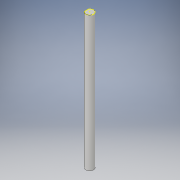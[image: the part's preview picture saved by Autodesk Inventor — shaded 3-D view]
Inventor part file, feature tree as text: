
AUTODESK INVENTOR PART (.ipt)
format: ipt  version: 2017 (Build 210142000, 142)  size: 114,688 bytes
history: native  units: in
note: dims shown in document units (in); Inventor stores cm internally (conversion verified against a paired STEP export)
features: move_body x3, sketch x2, direct_edit x2, chamfer x1, projected_geometry x1
ambient origin geometry x8: Origin, YZ Plane, XZ Plane, XY Plane, X Axis, Y Axis, Z Axis, Center Point
bodies: Solid1 (feature_tree)
feature tree (9):
  chamfer  "Chamfer1"  [1 undecoded]
  sketch  "Sketch1"  dims[d8=0.0in d9=0.0in d10=-0.284in]
  sketch  "Sketch2"  dims[d11=0.0in d12=0.0in d13=0.284in]
  direct_edit  "Direct Edit2"
  direct_edit  "Direct Edit3"
  projected_geometry  "Projected Loop1"
  move_body  "Move2"
  move_body  "Move3"
  move_body  "Move4"
note: 1 required parameter value undecoded (feature->parameter linkage not recoverable at this tier; creation-order binding heuristic only, values carry confidence <= 0.55)
